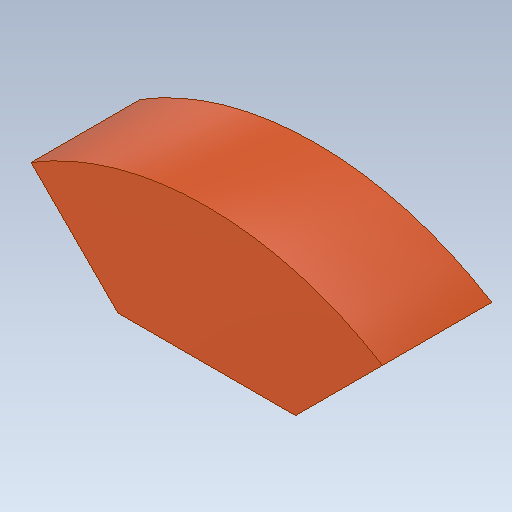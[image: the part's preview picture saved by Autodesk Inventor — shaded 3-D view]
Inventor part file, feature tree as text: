
AUTODESK INVENTOR PART (.ipt)
format: ipt  version: 2020 (Build 240168000, 168)  size: 169,472 bytes
history: native  units: mm
features: extrude x7, sketch x7, plane x4
ambient origin geometry x8: Origin, YZ Plane, XZ Plane, XY Plane, X Axis, Y Axis, Z Axis, Center Point
bodies: Solid1 (feature_tree)
feature tree (18):
  extrude  "Extrusion1"  Depth=90.0mm
  plane  "Work Plane1"
  extrude  "Extrusion2"  Depth=90.0mm
  plane  "Work Plane2"
  extrude  "Extrusion3"  TaperAngle=0.0deg  [1 undecoded]
  plane  "Work Plane3"
  extrude  "Extrusion4"  Depth=60.0mm
  plane  "Work Plane4"
  extrude  "Extrusion5"  TaperAngle=0.0deg  [1 undecoded]
  extrude  "Extrusion6"  Depth=70.0mm TaperAngle=0.0deg
  extrude  "Extrusion7"  Depth=80.0mm TaperAngle=0.0deg
  sketch  "Sketch1"  dims[d0=130.0mm d1=90.0mm]
  sketch  "Sketch2"  dims[d2=135.0deg d3=90.0mm]
  sketch  "Sketch4"  dims[d4=80.0mm d5=0.0mm d6=0.0mm]
  sketch  "Sketch5"  dims[d7=60.0mm d8=60.0mm]
  sketch  "Sketch6"  dims[d9=30.0mm d10=0.0mm d11=0.0mm]
  sketch  "Sketch7"  dims[d12=20.0mm d13=70.0mm d14=0.0mm]
  sketch  "Sketch8"  dims[d15=0.0mm d16=80.0mm d17=0.0mm d18=0.0mm d19=34.0mm d21=34.0mm d22=15.0mm d23=0.0mm d24=25.0mm d25=25.0mm d26=20.0mm d27=0.0mm d28=25.0mm d29=20.0mm d30=0.0mm]
note: 2 required parameter values undecoded (feature->parameter linkage not recoverable at this tier; creation-order binding heuristic only, values carry confidence <= 0.55)
